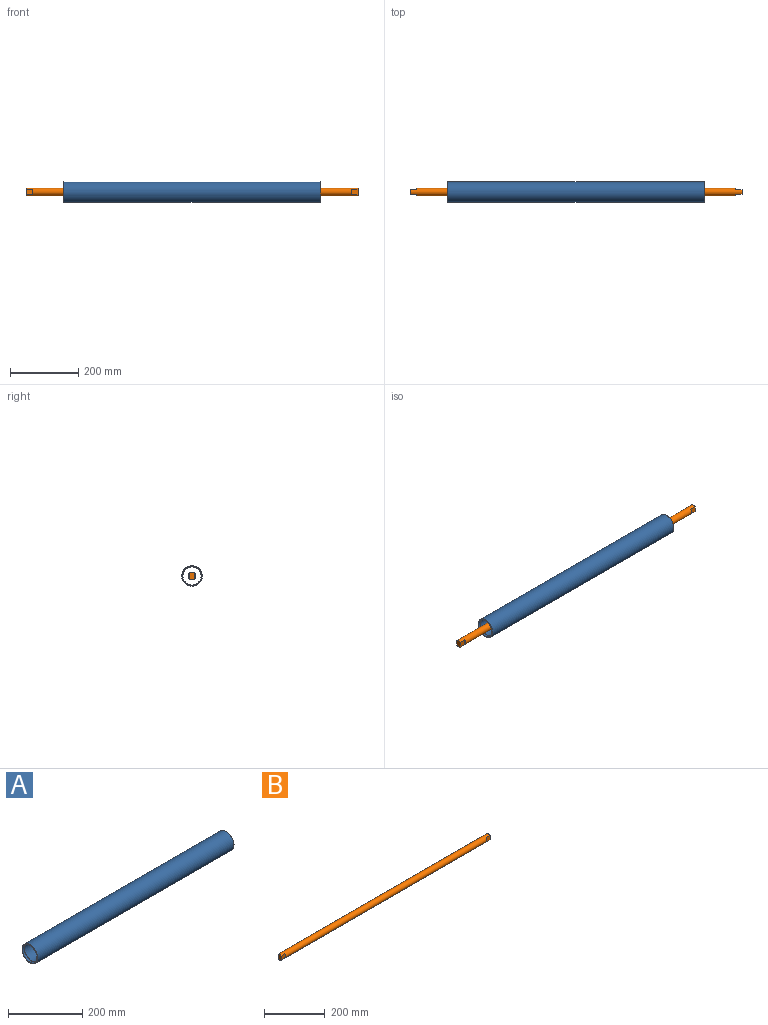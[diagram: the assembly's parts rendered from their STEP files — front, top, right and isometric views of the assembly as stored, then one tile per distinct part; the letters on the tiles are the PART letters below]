
ASSEMBLY  parts=2 mates=1
PART A: 10 faces, bbox 750x64.9x64.9 mm
  f0: cylinder r=26.5mm len=736mm, axis (-1,0,0), area 122547.2mm2, adj f5,f9
  f1: cylinder r=30mm len=748mm, axis (-1,0,0), area 140994.7mm2, adj f6,f7
  f2: plane 58x58mm, normal (1,0,0), area 266.2mm2, adj f6,f8
  f3: plane 58x58mm, normal (-1,0,0), area 266.2mm2, adj f4,f7
  f4: cylinder r=27.5mm len=55mm, axis (-1,0,0), area 1209.5mm2, adj f3,f5
  f5: plane 55x55mm, normal (-1,0,0), area 169.6mm2, adj f0,f4
  f6: torus R=29mm, axis (1,0,0), area 292.5mm2, adj f1,f2
  f7: torus R=29mm, axis (1,0,0), area 292.5mm2, adj f1,f3
  f8: cylinder r=27.5mm len=55mm, axis (1,0,0), area 1209.5mm2, adj f2,f9
  f9: plane 55x55mm, normal (1,0,0), area 169.6mm2, adj f0,f8
PART B: 11 faces, bbox 970x22x22 mm
  f0: plane 22x14mm, normal (-1,0,0), area 285.7mm2, adj f2,f7,f9
  f1: plane 22x14mm, normal (1,0,0), area 285.7mm2, adj f2,f3,f5
  f2: cylinder r=11mm len=970mm, axis (-1,0,0), area 65646mm2, adj f0,f1,f3,f4,f5,f6,f7,f8
  f3: plane 18x16.97mm, normal (0,-1,0), area 305.5mm2, adj f1,f2,f4
  f4: plane 16.97x4mm, normal (1,0,0), area 47.2mm2, adj f2,f3
  f5: plane 18x16.97mm, normal (0,1,0), area 305.5mm2, adj f1,f2,f6
  f6: plane 16.97x4mm, normal (1,0,0), area 47.2mm2, adj f2,f5
  f7: plane 18x16.97mm, normal (0,1,0), area 305.5mm2, adj f0,f2,f8
  f8: plane 16.97x4mm, normal (-1,0,0), area 47.2mm2, adj f2,f7
  f9: plane 18x16.97mm, normal (0,-1,0), area 305.5mm2, adj f0,f2,f10
  f10: plane 16.97x4mm, normal (-1,0,0), area 47.2mm2, adj f2,f9
PLACE A t=(0.62,0.3,0.09)mm
PLACE B t=(0.62,0.3,0.09)mm
MATE planar A.f1 <-> B.f2  axis (-1,0,0) through (0.62,0.3,0.09)mm
